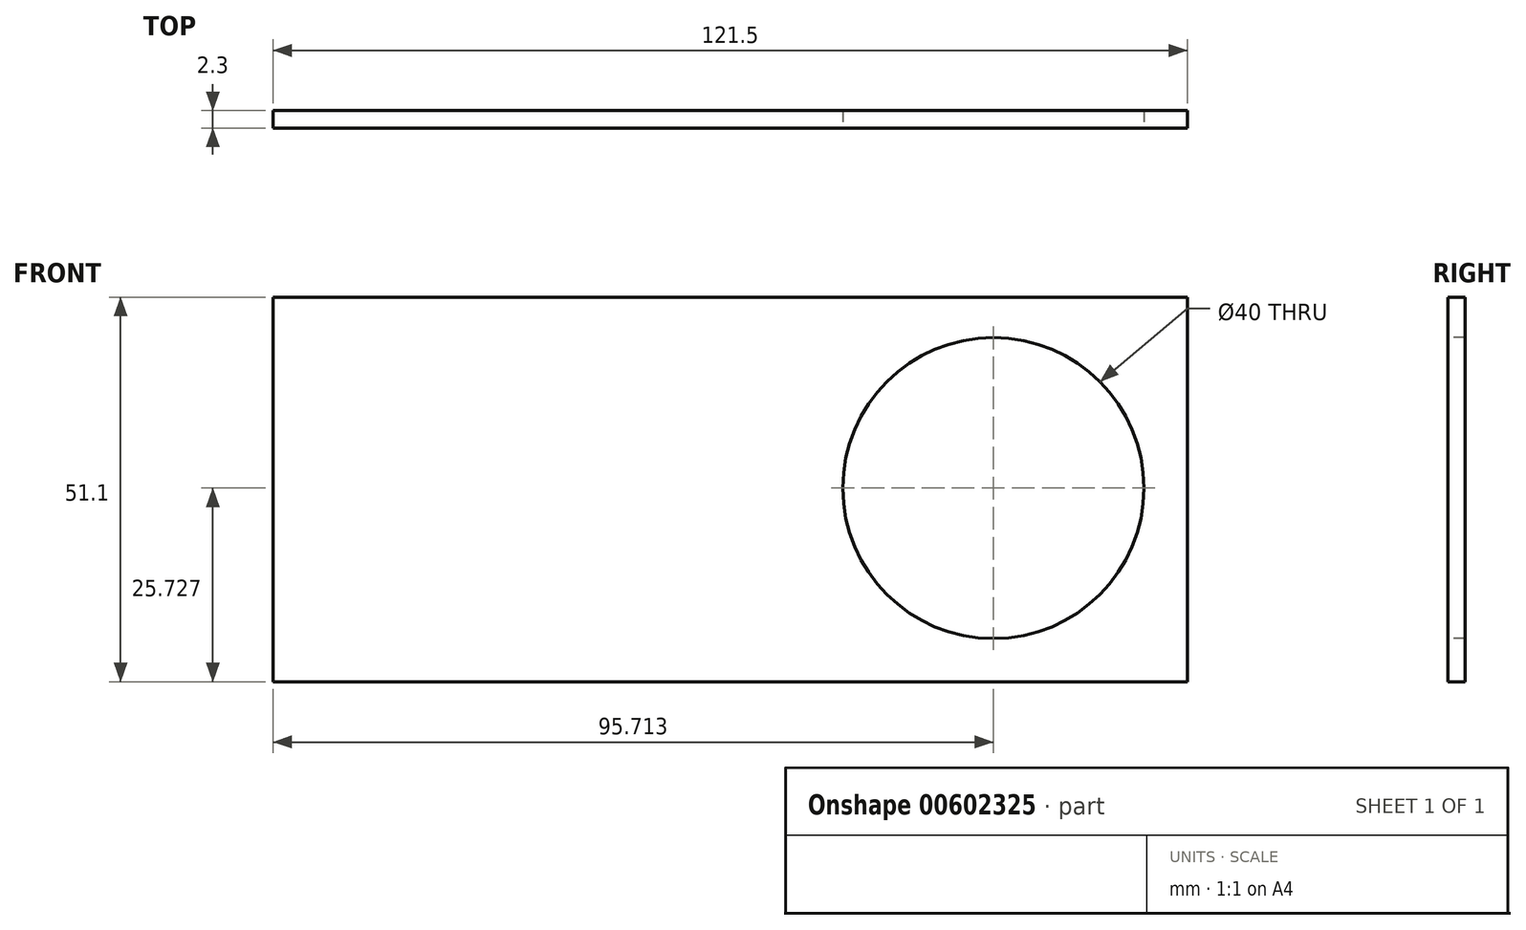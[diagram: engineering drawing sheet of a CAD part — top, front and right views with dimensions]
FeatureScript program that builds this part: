
annotation { "Feature Type Name" : "Feature", "Feature Type Description" : "" }
export const myFeature = defineFeature(function(context is Context, id is Id, definition is map)
    precondition{}
    {
        {
            var Q0;
            Q0=qCreatedBy(makeId("Front.planeOp"),FACE);
            var sketch = newSketch(context, id + "F0", { "sketchPlane" : qUnion([Q0])});
            skLineSegment(sketch, "E0.bottom", {"start": v(60.75, 6) * mm, "end": v(-60.75, 6) * mm});
            skLineSegment(sketch, "E0.top", {"start": v(60.75, -45.1) * mm, "end": v(-60.75, -45.1) * mm});
            skLineSegment(sketch, "E0.left", {"start": v(60.75, 6) * mm, "end": v(60.75, -45.1) * mm});
            skLineSegment(sketch, "E0.right", {"start": v(-60.75, 6) * mm, "end": v(-60.75, -45.1) * mm});
            skPoint(sketch, "E0.middle", {"position": v(0, -19.55) * mm});
            skSolve(sketch);
        }
        {
            var Q0;
            Q0=makeQuery(id+"F0.imprint","IMPRINT",FACE,{"disambiguationData":[TD([[makeQuery(id+"F0.imprint","IMPRINT",EDGE,{"derivedFrom":sQuery(id+"F0.wireOp",EDGE,"E0.bottom")}),1.0]])]});
            extrude(context, id + "F1", {"entities" : qUnion([Q0]), "depth" : 2.3 * mm, "offsetDistance" : 25 * mm});
        }
        {
            var Q0;
            Q0=makeQuery(id+"F1.opExtrude","CAP_FACE",FACE,{"disambiguationData":[OSD([sQuery(id+"F0.wireOp",EDGE,"E0.bottom"),sQuery(id+"F0.wireOp",EDGE,"E0.top"),sQuery(id+"F0.wireOp",EDGE,"E0.left"),sQuery(id+"F0.wireOp",EDGE,"E0.right")])],"isStart":false});
            var sketch = newSketch(context, id + "F2", { "sketchPlane" : qUnion([Q0])});
            skCircle(sketch, "E1", {"center": v(34.96, -19.37) * mm, "radius": 20 * mm});
            skSolve(sketch);
        }
        {
            var Q0;
            Q0 = qSketchRegion(id + "F2", true);
            extrude(context, id + "F3", {"entities" : qUnion([Q0]), "operationType" : NewBodyOperationType.REMOVE, "oppositeDirection" : true, "depth" : 25 * mm, "offsetDistance" : 25 * mm});
        }
    });
